# Revit family: equip-sink-elkay-rigidbilt-TPL
name_source: partatom
category: Plumbing Fixtures
units: mm (PartAtom-declared; Revit-internal decimal feet)

## family parameters
Always vertical = Yes
Cut with Voids When Loaded = No
Part Type = Normal
Room Calculation Point = No
Round Connector Dimension = Use Diameter
Shared = No
Work Plane-Based = No

## types (1)
- ByType
    Backsplash Height = 0' - 6 1/4"
    Backsplash Width = 0' - 2"
    Compartment Depth = 1' - 0 3/4"
    Compartment Length = 1' - 6"
    Compartment Width = 2' - 0"
    Description = Rigidbilt Scullery Sinks, Triple Compartment
    Drainboard Left = 0' - 4 1/2"
    Drainboard Right = 0' - 4 1/2"
    Faucet CL from Top Backsplash = 0' - 4 1/2"
    Hidden Compartment Length = 1' - 6"
    Hidden Compartment Width = 2' - 0"
    Hidden Drainboard Left = 0' - 3"
    Hidden Drainboard Right = 0' - 3"
    Hidden Length = 5' - 7 1/2"
    Hidden Width = 2' - 5 3/4"
    Hole 1 From CL = 0' - 4"
    Hole 1 to 2 = 0' - 8"
    Length = 5' - 7 1/2"
    Manufacturer = Elkay Manufacturer
    Model = Rigidbilt
    Rim Height = 3' - 0"
    Sink Drain Location = 1' - 0"
    Sink Ledge Back Width = 0' - 1 1/8"
    Sink Ledge DB Left Side Width = 0' - 3"
    Sink Ledge DB Right Side Width = 0' - 3"
    Sink Ledge Front Width = 0' - 1 1/8"
    Sink Ledge Middle = 0' - 2 1/4"
    Sink Material = Metal - Steel - Stainless - Chrome
    Sink Rim Front Width = 0' - 1 1/2"
    Sink Rim Sides Width = 0' - 1 1/2"
    Specification URL = http://www.elkayusa.com
    URL = www.elkayusa.com
    Width = 2' - 5 3/4"

## geometry (parser evidence)
native form markers: Sweep x5
no freeform markers — native parametric forms only
